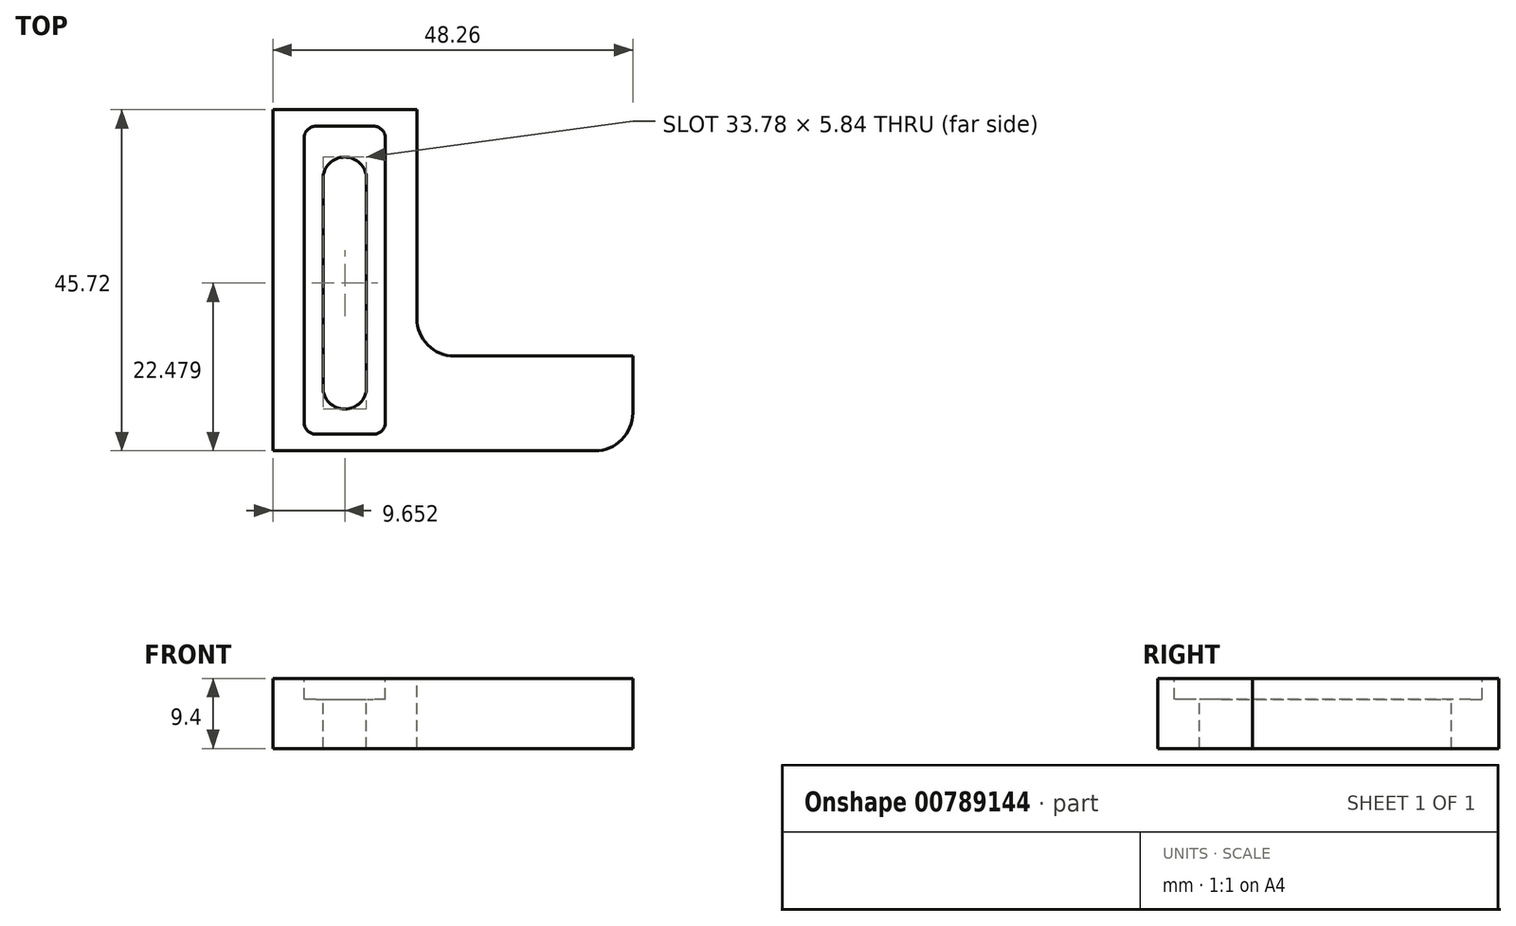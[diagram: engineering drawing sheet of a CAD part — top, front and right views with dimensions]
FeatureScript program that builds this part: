
annotation { "Feature Type Name" : "Feature", "Feature Type Description" : "" }
export const myFeature = defineFeature(function(context is Context, id is Id, definition is map)
    precondition{}
    {
        {
            var Q0;
            Q0=qCreatedBy(makeId("Top.planeOp"),FACE);
            var sketch = newSketch(context, id + "F0", { "sketchPlane" : qUnion([Q0])});
            skLineSegment(sketch, "E0.bottom", {"start": v(0, 0) * mm, "end": v(48.26, 0) * mm});
            skLineSegment(sketch, "E0.top", {"start": v(0, 45.72) * mm, "end": v(48.26, 45.72) * mm});
            skLineSegment(sketch, "E0.left", {"start": v(0, 0) * mm, "end": v(0, 45.72) * mm});
            skLineSegment(sketch, "E0.right", {"start": v(48.26, 0) * mm, "end": v(48.26, 45.72) * mm});
            skSolve(sketch);
        }
        {
            var Q0;
            Q0 = qSketchRegion(id + "F0", true);
            extrude(context, id + "F1", {"entities" : qUnion([Q0]), "depth" : 9.4 * mm, "offsetDistance" : 25.4 * mm});
        }
        {
            var Q0;
            Q0=makeQuery(id+"F1.opExtrude","CAP_FACE",FACE,{"disambiguationData":[OSD([sQuery(id+"F0.wireOp",EDGE,"E0.bottom"),sQuery(id+"F0.wireOp",EDGE,"E0.top"),sQuery(id+"F0.wireOp",EDGE,"E0.left"),sQuery(id+"F0.wireOp",EDGE,"E0.right")])],"isStart":false});
            var sketch = newSketch(context, id + "F2", { "sketchPlane" : qUnion([Q0])});
            skLineSegment(sketch, "E1.bottom", {"start": v(48.26, 45.72) * mm, "end": v(19.3, 45.72) * mm});
            skLineSegment(sketch, "E1.top", {"start": v(48.26, 12.7) * mm, "end": v(19.3, 12.7) * mm});
            skLineSegment(sketch, "E1.left", {"start": v(48.26, 45.72) * mm, "end": v(48.26, 12.7) * mm});
            skLineSegment(sketch, "E1.right", {"start": v(19.3, 45.72) * mm, "end": v(19.3, 12.7) * mm});
            skSolve(sketch);
        }
        {
            var Q0;
            Q0 = qSketchRegion(id + "F2", true);
            extrude(context, id + "F3", {"entities" : qUnion([Q0]), "operationType" : NewBodyOperationType.REMOVE, "oppositeDirection" : true, "depth" : 25.4 * mm, "offsetDistance" : 25.4 * mm});
        }
        {
            var Q0;
            Q0=makeQuery(id+"F1.opExtrude","CAP_FACE",FACE,{"disambiguationData":[OSD([sQuery(id+"F0.wireOp",EDGE,"E0.bottom"),sQuery(id+"F0.wireOp",EDGE,"E0.top"),sQuery(id+"F0.wireOp",EDGE,"E0.left"),sQuery(id+"F0.wireOp",EDGE,"E0.right")])],"isStart":false});
            var sketch = newSketch(context, id + "F4", { "sketchPlane" : qUnion([Q0])});
            skLineSegment(sketch, "E2.bottom", {"start": v(4.2, 43.5) * mm, "end": v(15.11, 43.5) * mm});
            skLineSegment(sketch, "E2.top", {"start": v(4.2, 2.22) * mm, "end": v(15.11, 2.22) * mm});
            skLineSegment(sketch, "E2.left", {"start": v(4.2, 43.5) * mm, "end": v(4.2, 2.22) * mm});
            skLineSegment(sketch, "E2.right", {"start": v(15.11, 43.5) * mm, "end": v(15.11, 2.22) * mm});
            skSolve(sketch);
        }
        {
            var Q0;
            Q0 = qSketchRegion(id + "F4", true);
            extrude(context, id + "F5", {"entities" : qUnion([Q0]), "operationType" : NewBodyOperationType.REMOVE, "oppositeDirection" : true, "depth" : 2.8 * mm, "offsetDistance" : 25.4 * mm});
        }
        {
            var Q0;
            Q0=makeQuery(id+"F5.boolean.opBoolean","COPY",FACE,{"derivedFrom":makeQuery(id+"F5.opExtrude","CAP_FACE",FACE,{"disambiguationData":[OSD([sQuery(id+"F4.wireOp",EDGE,"E2.bottom"),sQuery(id+"F4.wireOp",EDGE,"E2.top"),sQuery(id+"F4.wireOp",EDGE,"E2.left"),sQuery(id+"F4.wireOp",EDGE,"E2.right")])],"isStart":false})});
            var sketch = newSketch(context, id + "F6", { "sketchPlane" : qUnion([Q0])});
            skLineSegment(sketch, "E3", {"start": v(6.73, 36.45) * mm, "end": v(6.73, 8.5) * mm});
            skLineSegment(sketch, "E4", {"start": v(12.57, 8.5) * mm, "end": v(12.57, 36.45) * mm});
            skArc(sketch, "E5", {"start": v(6.73, 36.45) * mm, "mid": v(9.65, 39.37) * mm, "end": v(12.57, 36.45) * mm});
            skArc(sketch, "E6", {"start": v(12.57, 8.5) * mm, "mid": v(9.65, 5.59) * mm, "end": v(6.73, 8.5) * mm});
            skSolve(sketch);
        }
        {
            var Q0;
            Q0 = qSketchRegion(id + "F6", true);
            extrude(context, id + "F7", {"entities" : qUnion([Q0]), "operationType" : NewBodyOperationType.REMOVE, "endBound" : BoundingType.THROUGH_ALL, "oppositeDirection" : true, "depth" : 25.4 * mm, "offsetDistance" : 25.4 * mm});
        }
        {
            var Q0;
            Q0=makeQuery(id+"F3.boolean.opBoolean","COPY",EDGE,{"derivedFrom":makeQuery(id+"F3.opExtrude","SWEPT_EDGE",EDGE,{"disambiguationData":[OSD([sQuery(id+"F2.wireOp",EDGE,"E1.top"),sQuery(id+"F2.wireOp",EDGE,"E1.right")])]})});
            fillet(context, id + "F8", {"entities" : qUnion([Q0]), "radius" : 5.08 * mm, "tangentPropagation" : true, "allowEdgeOverflow" : false});
        }
        {
            var Q0;
            Q0=makeQuery(id+"F5.boolean.opBoolean","COPY",EDGE,{"derivedFrom":makeQuery(id+"F5.opExtrude","SWEPT_EDGE",EDGE,{"disambiguationData":[OSD([sQuery(id+"F4.wireOp",EDGE,"E2.bottom"),sQuery(id+"F4.wireOp",EDGE,"E2.left")])]})});
            var Q1;
            Q1=makeQuery(id+"F5.boolean.opBoolean","COPY",EDGE,{"derivedFrom":makeQuery(id+"F5.opExtrude","SWEPT_EDGE",EDGE,{"disambiguationData":[OSD([sQuery(id+"F4.wireOp",EDGE,"E2.top"),sQuery(id+"F4.wireOp",EDGE,"E2.left")])]})});
            var Q2;
            Q2=makeQuery(id+"F5.boolean.opBoolean","COPY",EDGE,{"derivedFrom":makeQuery(id+"F5.opExtrude","SWEPT_EDGE",EDGE,{"disambiguationData":[OSD([sQuery(id+"F4.wireOp",EDGE,"E2.top"),sQuery(id+"F4.wireOp",EDGE,"E2.right")])]})});
            var Q3;
            Q3=makeQuery(id+"F5.boolean.opBoolean","COPY",EDGE,{"derivedFrom":makeQuery(id+"F5.opExtrude","SWEPT_EDGE",EDGE,{"disambiguationData":[OSD([sQuery(id+"F4.wireOp",EDGE,"E2.bottom"),sQuery(id+"F4.wireOp",EDGE,"E2.right")])]})});
            fillet(context, id + "F9", {"entities" : qUnion([Q0, Q1, Q2, Q3]), "radius" : 1.59 * mm, "tangentPropagation" : true, "allowEdgeOverflow" : false});
        }
        {
            var Q0;
            Q0=makeQuery(id+"F1.opExtrude","SWEPT_EDGE",EDGE,{"disambiguationData":[OSD([sQuery(id+"F0.wireOp",EDGE,"E0.bottom"),sQuery(id+"F0.wireOp",EDGE,"E0.right")])]});
            var Q1;
            Q1=makeQuery(id+"F3.boolean.opBoolean","COPY",EDGE,{"derivedFrom":makeQuery(id+"F3.opExtrude","SWEPT_EDGE",EDGE,{"disambiguationData":[OSD([sQuery(id+"F0.wireOp",EDGE,"E0.right"),sQuery(id+"F2.wireOp",EDGE,"E1.top"),sQuery(id+"F2.wireOp",EDGE,"E1.left")])]})});
            fillet(context, id + "F10", {"entities" : qUnion([Q0, Q1]), "radius" : 5.08 * mm, "tangentPropagation" : true, "allowEdgeOverflow" : false});
        }
    });
